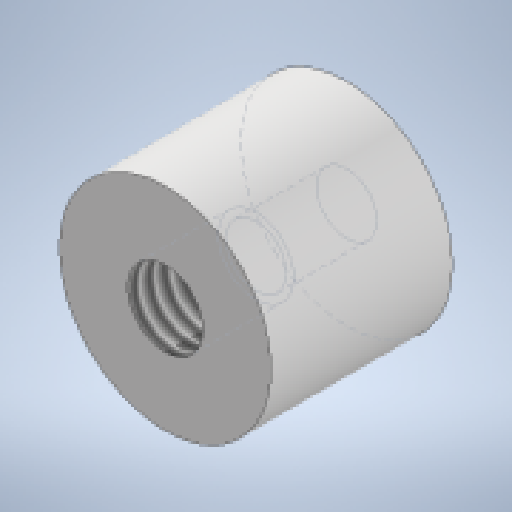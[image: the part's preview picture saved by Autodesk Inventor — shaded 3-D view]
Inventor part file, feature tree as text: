
AUTODESK INVENTOR PART (.ipt)
format: ipt  version: 2023 (Build 270158000, 158)  size: 157,184 bytes
history: native  units: mm
features: extrude x2, thread x2, sketch x2
ambient origin geometry x8: Origin, YZ Plane, XZ Plane, XY Plane, X Axis, Y Axis, Z Axis, Center Point
bodies: Solid1 (feature_tree)
feature tree (6):
  extrude  "Extrusion1"  Depth=2.0mm
  extrude  "Extrusion2"  Depth=3.0mm
  thread  "Thread1"  [1 undecoded]
  thread  "Thread2"  [1 undecoded]
  sketch  "Sketch1"  dims[d0=7.0mm d1=2.0mm]
  sketch  "Sketch2"  dims[d2=6.0mm d3=0.0mm d4=2.5mm d5=3.0mm d6=0.0mm d7=3.0mm d8=0.0mm d9=3.0mm d10=0.0mm]
note: 2 required parameter values undecoded (feature->parameter linkage not recoverable at this tier; creation-order binding heuristic only, values carry confidence <= 0.55)
